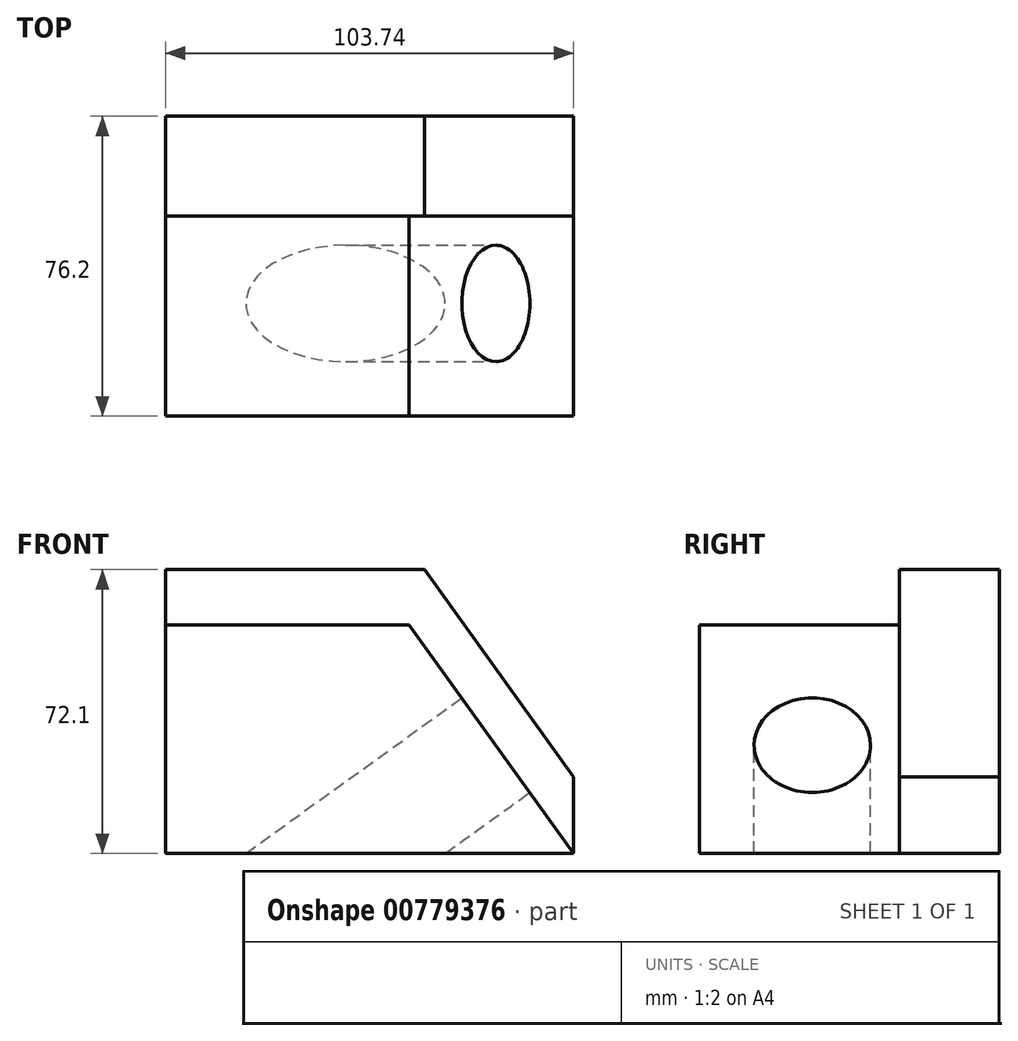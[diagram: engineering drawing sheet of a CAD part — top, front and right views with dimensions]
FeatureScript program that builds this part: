
annotation { "Feature Type Name" : "Feature", "Feature Type Description" : "" }
export const myFeature = defineFeature(function(context is Context, id is Id, definition is map)
    precondition{}
    {
        {
            var Q0;
            Q0=qCreatedBy(makeId("Front.planeOp"),FACE);
            var sketch = newSketch(context, id + "F0", { "sketchPlane" : qUnion([Q0])});
            skLineSegment(sketch, "E0.bottom", {"start": v(-51.87, 36.05) * mm, "end": v(14, 36.05) * mm});
            skLineSegment(sketch, "E0.top", {"start": v(-51.87, -36.05) * mm, "end": v(51.87, -36.05) * mm});
            skLineSegment(sketch, "E0.left", {"start": v(-51.87, 36.05) * mm, "end": v(-51.87, -36.05) * mm});
            skLineSegment(sketch, "E0.right", {"start": v(51.87, -16.58) * mm, "end": v(51.87, -36.05) * mm});
            skPoint(sketch, "E0.middle", {"position": v(0, 0) * mm});
            skLineSegment(sketch, "E1", {"start": v(10.09, 22.03) * mm, "end": v(51.87, -36.05) * mm});
            skLineSegment(sketch, "E2", {"start": v(14, 36.05) * mm, "end": v(51.87, -16.58) * mm});
            skLineSegment(sketch, "E3", {"start": v(10.09, 22.03) * mm, "end": v(-51.87, 22.03) * mm});
            skPoint(sketch, "E4.orphan", {"position": v(0, 36.05) * mm});
            skPoint(sketch, "E5.orphan", {"position": v(51.87, 36.05) * mm});
            skSolve(sketch);
        }
        {
            var Q0;
            {var subQ0=sQuery(id+"F0.wireOp",EDGE,"E0.top");Q0=makeQuery(id+"F0.imprint","IMPRINT",FACE,{"disambiguationData":[TD([[makeQuery(id+"F0.imprint","IMPRINT",EDGE,{"derivedFrom":subQ0}),1.0]])]});}
            extrude(context, id + "F1", {"entities" : qUnion([Q0]), "depth" : 76.2 * mm, "offsetDistance" : 25.4 * mm});
        }
        {
            var Q0;
            Q0 = qSketchRegion(id + "F0", true);
            extrude(context, id + "F2", {"entities" : qUnion([Q0]), "operationType" : NewBodyOperationType.ADD, "depth" : 25.4 * mm, "offsetDistance" : 25.4 * mm});
        }
        {
            var Q0;
            Q0=makeQuery(id+"F1.opExtrude","SWEPT_FACE",FACE,{"disambiguationData":[OSD([sQuery(id+"F0.wireOp",EDGE,"E1")])]});
            var sketch = newSketch(context, id + "F3", { "sketchPlane" : qUnion([Q0])});
            skCircle(sketch, "E6", {"center": v(-47.59, -25.7) * mm, "radius": 14.79 * mm});
            skSolve(sketch);
        }
        {
            var Q0;
            Q0=makeQuery(id+"F3.imprint","IMPRINT",FACE,{"disambiguationData":[TD([[makeQuery(id+"F3.imprint","IMPRINT",EDGE,{"derivedFrom":sQuery(id+"F3.wireOp",EDGE,"E6")}),1.0]])]});
            extrude(context, id + "F4", {"entities" : qUnion([Q0]), "operationType" : NewBodyOperationType.REMOVE, "endBound" : BoundingType.THROUGH_ALL, "oppositeDirection" : true, "depth" : 25.4 * mm, "offsetDistance" : 25.4 * mm});
        }
    });
